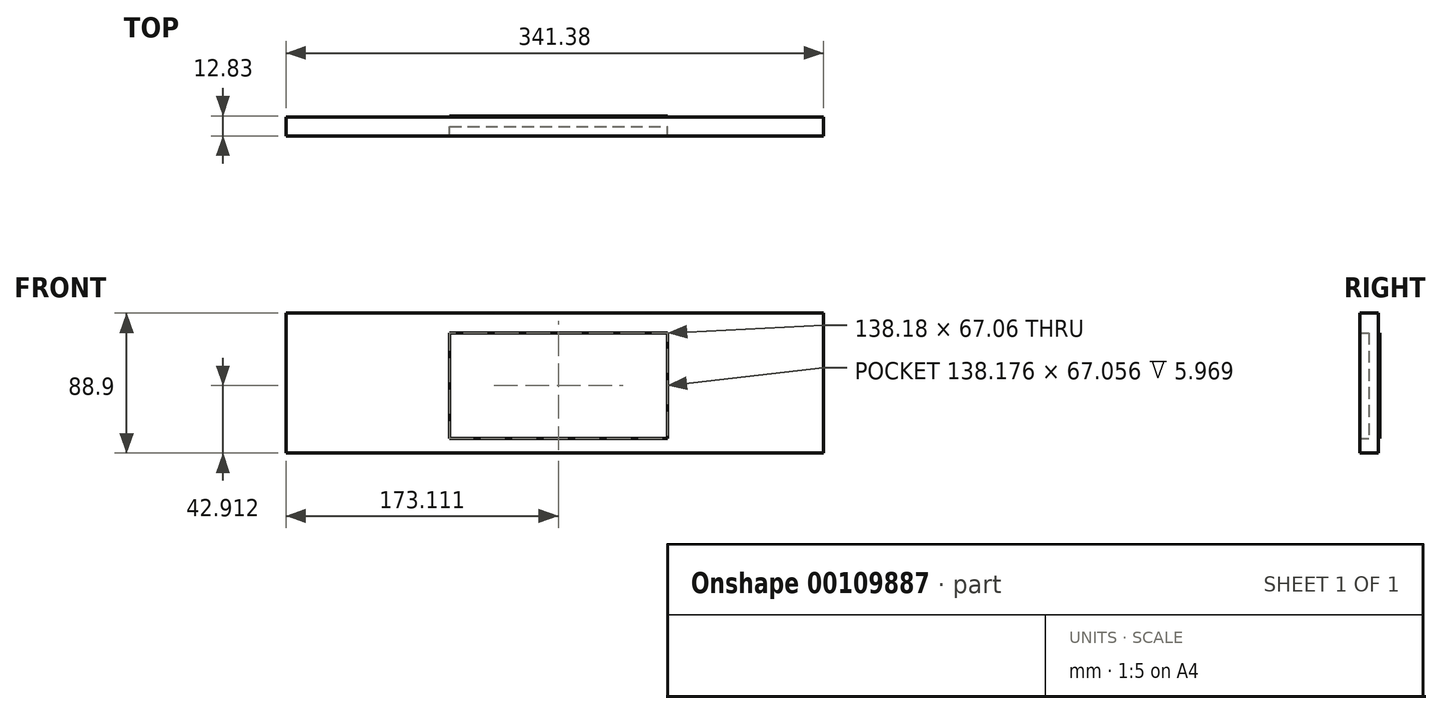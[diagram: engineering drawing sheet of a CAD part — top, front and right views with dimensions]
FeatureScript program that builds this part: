
annotation { "Feature Type Name" : "Feature", "Feature Type Description" : "" }
export const myFeature = defineFeature(function(context is Context, id is Id, definition is map)
    precondition{}
    {
        {
            var Q0;
            Q0=qCreatedBy(makeId("Front.planeOp"),FACE);
            var sketch = newSketch(context, id + "F0", { "sketchPlane" : qUnion([Q0])});
            skLineSegment(sketch, "E0.bottom", {"start": v(-66.87, 37.15) * mm, "end": v(71.3, 37.15) * mm});
            skLineSegment(sketch, "E0.top", {"start": v(-66.87, -29.9) * mm, "end": v(71.3, -29.9) * mm});
            skLineSegment(sketch, "E0.left", {"start": v(-66.87, 37.15) * mm, "end": v(-66.87, -29.9) * mm});
            skLineSegment(sketch, "E0.right", {"start": v(71.3, 37.15) * mm, "end": v(71.3, -29.9) * mm});
            skSolve(sketch);
        }
        {
            var Q0;
            Q0=makeQuery(id+"F0.imprint","IMPRINT",FACE,{"disambiguationData":[TD([[makeQuery(id+"F0.imprint","IMPRINT",EDGE,{"derivedFrom":sQuery(id+"F0.wireOp",EDGE,"E0.bottom")}),-1.0]])]});
            var sketch = newSketch(context, id + "F1", { "sketchPlane" : qUnion([Q0])});
            skLineSegment(sketch, "E1.bottom", {"start": v(-170.9, 49.6) * mm, "end": v(170.49, 49.6) * mm});
            skLineSegment(sketch, "E1.top", {"start": v(-170.9, -39.3) * mm, "end": v(170.49, -39.3) * mm});
            skLineSegment(sketch, "E1.left", {"start": v(-170.9, 49.6) * mm, "end": v(-170.9, -39.3) * mm});
            skLineSegment(sketch, "E1.right", {"start": v(170.49, 49.6) * mm, "end": v(170.49, -39.3) * mm});
            skSolve(sketch);
        }
        {
            var Q0;
            Q0=makeQuery(id+"F1.imprint","IMPRINT",FACE,{"disambiguationData":[TD([[makeQuery(id+"F1.imprint","IMPRINT",EDGE,{"derivedFrom":sQuery(id+"F1.wireOp",EDGE,"E1.bottom")}),-1.0]])]});
            extrude(context, id + "F2", {"entities" : qUnion([Q0]), "endBound" : BoundingType.SYMMETRIC, "depth" : 11.94 * mm});
        }
        {
            var Q0;
            Q0 = qSketchRegion(id + "F0", true);
            extrude(context, id + "F3", {"entities" : qUnion([Q0]), "operationType" : NewBodyOperationType.ADD, "oppositeDirection" : true, "depth" : 6.86 * mm});
        }
    });
